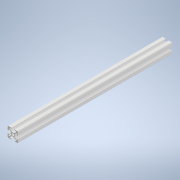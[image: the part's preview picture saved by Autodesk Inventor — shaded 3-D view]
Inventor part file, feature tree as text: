
AUTODESK INVENTOR PART (.ipt)
format: ipt  version: 2022 (Build 260153000, 153)  size: 244,736 bytes
history: native  units: mm
features: extrude x1, sketch x1
ambient origin geometry x8: Origin, YZ Plane, XZ Plane, XY Plane, X Axis, Y Axis, Z Axis, Center Point
bodies: Solid1 (feature_tree)
feature tree (2):
  extrude  "Extrusion1"  Depth=301.4mm
  sketch  "Sketch_1"  dims[d0=301.4mm d1=0.0mm d2=0.5mm d3=0.872665mm d4=0.5mm d5=0.872665mm]
